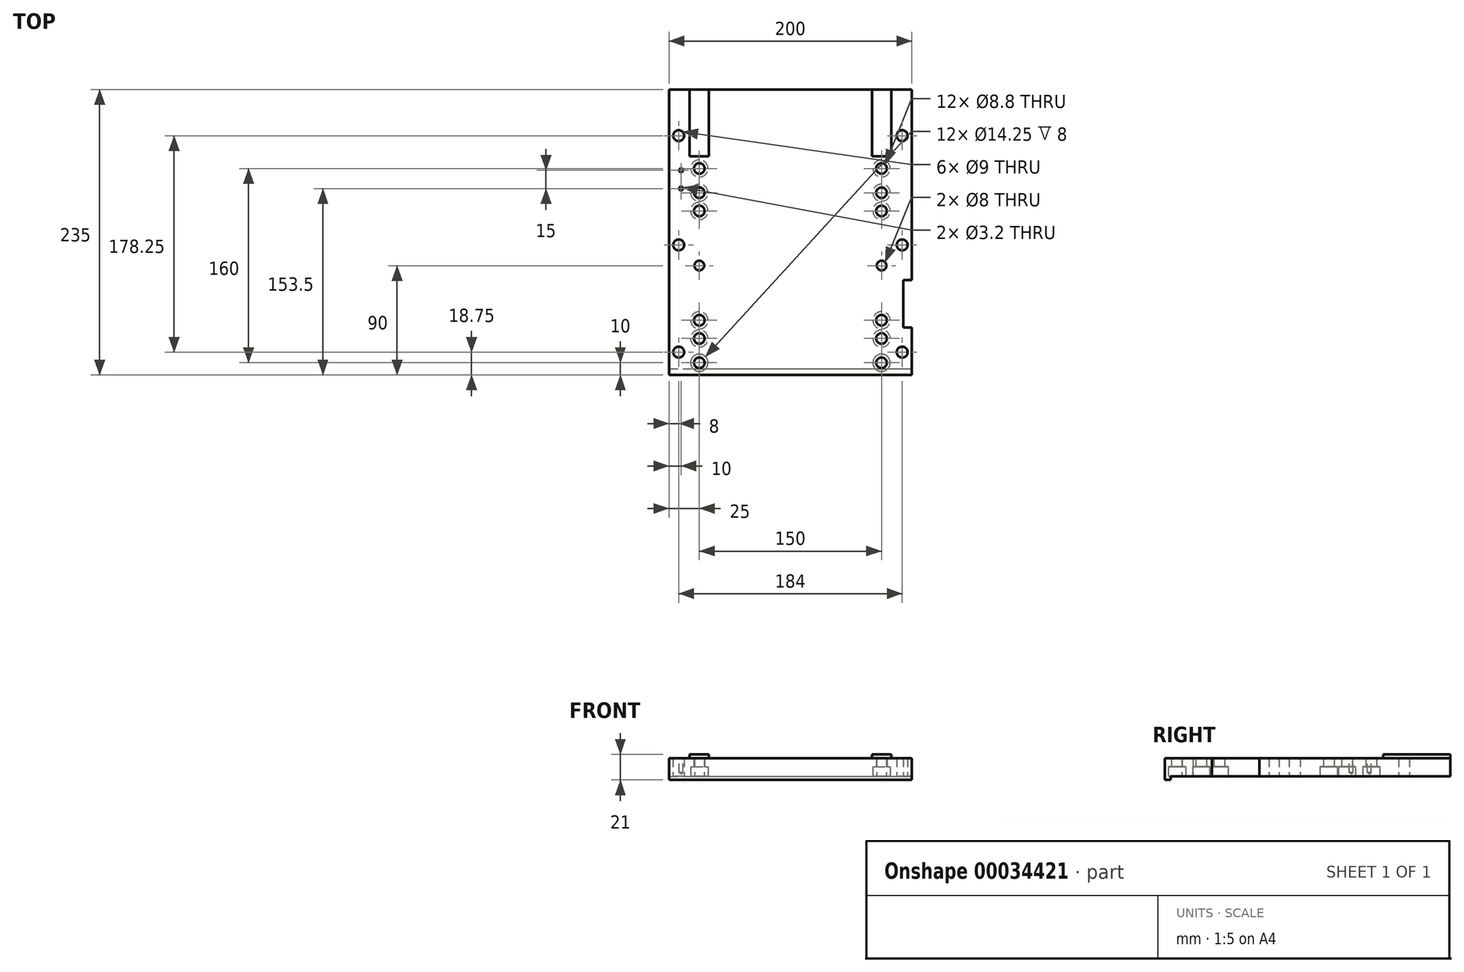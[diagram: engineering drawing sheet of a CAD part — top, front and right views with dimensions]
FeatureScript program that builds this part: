
annotation { "Feature Type Name" : "Feature", "Feature Type Description" : "" }
export const myFeature = defineFeature(function(context is Context, id is Id, definition is map)
    precondition{}
    {
        {
            var Q0;
            Q0=qCreatedBy(makeId("Top.planeOp"),FACE);
            var sketch = newSketch(context, id + "F0", { "sketchPlane" : qUnion([Q0])});
            skLineSegment(sketch, "E0", {"start": v(-100, 117.5) * mm, "end": v(100, 117.5) * mm});
            skLineSegment(sketch, "E1", {"start": v(-100, -117.5) * mm, "end": v(100, -117.5) * mm});
            skLineSegment(sketch, "E2", {"start": v(-100, -117.5) * mm, "end": v(-100, 117.5) * mm});
            skLineSegment(sketch, "E3", {"start": v(93, -78.5) * mm, "end": v(100, -78.5) * mm});
            skLineSegment(sketch, "E4", {"start": v(93, -39.5) * mm, "end": v(93, -78.5) * mm});
            skLineSegment(sketch, "E5", {"start": v(100, -39.5) * mm, "end": v(100, 117.5) * mm});
            skLineSegment(sketch, "E6", {"start": v(100, -117.5) * mm, "end": v(100, -78.5) * mm});
            skLineSegment(sketch, "E7", {"start": v(100, -39.5) * mm, "end": v(93, -39.5) * mm});
            skCircle(sketch, "E8", {"center": v(75, -27.5) * mm, "radius": 4 * mm});
            skCircle(sketch, "E9", {"center": v(92, -98.75) * mm, "radius": 4.5 * mm});
            skCircle(sketch, "E10", {"center": v(92, -10.5) * mm, "radius": 4.5 * mm});
            skCircle(sketch, "E11", {"center": v(92, 79.5) * mm, "radius": 4.5 * mm});
            skCircle(sketch, "E12", {"center": v(-92, 79.5) * mm, "radius": 4.5 * mm});
            skCircle(sketch, "E13", {"center": v(-92, -10.5) * mm, "radius": 4.5 * mm});
            skCircle(sketch, "E14", {"center": v(-92, -98.75) * mm, "radius": 4.5 * mm});
            skCircle(sketch, "E15", {"center": v(-75, -27.5) * mm, "radius": 4 * mm});
            skLineSegment(sketch, "E16", {"start": v(-83, 62.5) * mm, "end": v(-67, 62.5) * mm});
            skLineSegment(sketch, "E17", {"start": v(83, 117.5) * mm, "end": v(83, 62.5) * mm});
            skLineSegment(sketch, "E18", {"start": v(-83, 117.5) * mm, "end": v(-83, 62.5) * mm});
            skLineSegment(sketch, "E19", {"start": v(-100, -112.5) * mm, "end": v(100, -112.5) * mm});
            skLineSegment(sketch, "E20", {"start": v(-67, 117.5) * mm, "end": v(-67, 62.5) * mm});
            skLineSegment(sketch, "E21", {"start": v(67, 117.5) * mm, "end": v(67, 62.5) * mm});
            skLineSegment(sketch, "E22", {"start": v(67, 62.5) * mm, "end": v(83, 62.5) * mm});
            skSolve(sketch);
        }
        {
            var Q0;
            {var subQ7=sQuery(id+"F0.wireOp",EDGE,"E3");Q0=makeQuery(id+"F0.imprint","IMPRINT",FACE,{"disambiguationData":[TD([[makeQuery(id+"F0.imprint","IMPRINT",EDGE,{"derivedFrom":subQ7}),-1.0]])]});}
            var Q1;
            {var subQ0=sQuery(id+"F0.wireOp",EDGE,"E1");Q1=makeQuery(id+"F0.imprint","IMPRINT",FACE,{"disambiguationData":[TD([[makeQuery(id+"F0.imprint","IMPRINT",EDGE,{"derivedFrom":subQ0}),1.0]])]});}
            var Q2;
            Q2=makeQuery(id+"F0.imprint","IMPRINT",FACE,{"disambiguationData":[TD([[makeQuery(id+"F0.imprint","IMPRINT",EDGE,{"derivedFrom":sQuery(id+"F0.wireOp",EDGE,"E16")}),1.0]])]});
            var Q3;
            {var subQ0=sQuery(id+"F0.wireOp",EDGE,"E17");Q3=makeQuery(id+"F0.imprint","IMPRINT",FACE,{"disambiguationData":[TD([[makeQuery(id+"F0.imprint","IMPRINT",EDGE,{"derivedFrom":subQ0}),-1.0]])]});}
            extrude(context, id + "F1", {"entities" : qUnion([Q0, Q1, Q2, Q3]), "depth" : 15 * mm});
        }
        {
            var Q0;
            {var subQ0=sQuery(id+"F0.wireOp",EDGE,"E1");Q0=makeQuery(id+"F0.imprint","IMPRINT",FACE,{"disambiguationData":[TD([[makeQuery(id+"F0.imprint","IMPRINT",EDGE,{"derivedFrom":subQ0}),1.0]])]});}
            extrude(context, id + "F2", {"entities" : qUnion([Q0]), "operationType" : NewBodyOperationType.ADD, "oppositeDirection" : true, "depth" : 3 * mm});
        }
        {
            var Q0;
            {var subQ0=sQuery(id+"F0.wireOp",EDGE,"E17");Q0=makeQuery(id+"F0.imprint","IMPRINT",FACE,{"disambiguationData":[TD([[makeQuery(id+"F0.imprint","IMPRINT",EDGE,{"derivedFrom":subQ0}),-1.0]])]});}
            var Q1;
            Q1=makeQuery(id+"F0.imprint","IMPRINT",FACE,{"disambiguationData":[TD([[makeQuery(id+"F0.imprint","IMPRINT",EDGE,{"derivedFrom":sQuery(id+"F0.wireOp",EDGE,"E16")}),1.0]])]});
            extrude(context, id + "F3", {"entities" : qUnion([Q0, Q1]), "operationType" : NewBodyOperationType.ADD, "depth" : 18 * mm});
        }
        {
            var Q0;
            {var subQ7=sQuery(id+"F0.wireOp",EDGE,"E3");Q0=makeQuery(id+"F0.imprint","IMPRINT",FACE,{"disambiguationData":[TD([[makeQuery(id+"F0.imprint","IMPRINT",EDGE,{"derivedFrom":subQ7}),-1.0]])]});}
            var sketch = newSketch(context, id + "F4", { "sketchPlane" : qUnion([Q0])});
            skLineSegment(sketch, "E23.0", {"start": v(-100, -117.5) * mm, "end": v(100, -117.5) * mm, "construction": true});
            skLineSegment(sketch, "E24.0", {"start": v(100, -117.5) * mm, "end": v(100, -78.5) * mm, "construction": true});
            skPoint(sketch, "E25", {"position": v(75, -107.5) * mm});
            skPoint(sketch, "E26", {"position": v(75, -87.5) * mm});
            skPoint(sketch, "E27", {"position": v(75, -72.5) * mm});
            skPoint(sketch, "E28", {"position": v(-75, -107.5) * mm});
            skPoint(sketch, "E29", {"position": v(-75, -87.5) * mm});
            skPoint(sketch, "E30", {"position": v(-75, -72.5) * mm});
            skPoint(sketch, "E31", {"position": v(75, 17.5) * mm});
            skPoint(sketch, "E32", {"position": v(75, 32.5) * mm});
            skPoint(sketch, "E33", {"position": v(75, 52.5) * mm});
            skPoint(sketch, "E34", {"position": v(-75, 52.5) * mm});
            skPoint(sketch, "E35", {"position": v(-75, 32.5) * mm});
            skPoint(sketch, "E36", {"position": v(-75, 17.5) * mm});
            skSolve(sketch);
        }
        {
            var Q0;
            Q0=sQuery(id+"F4.wireOp",VERTEX,"E25");
            var Q1;
            Q1=sQuery(id+"F4.wireOp",VERTEX,"E26");
            var Q2;
            Q2=sQuery(id+"F4.wireOp",VERTEX,"E27");
            var Q3;
            Q3=sQuery(id+"F4.wireOp",VERTEX,"E31");
            var Q4;
            Q4=sQuery(id+"F4.wireOp",VERTEX,"E32");
            var Q5;
            Q5=sQuery(id+"F4.wireOp",VERTEX,"E33");
            var Q6;
            Q6=sQuery(id+"F4.wireOp",VERTEX,"E34");
            var Q7;
            Q7=sQuery(id+"F4.wireOp",VERTEX,"E35");
            var Q8;
            Q8=sQuery(id+"F4.wireOp",VERTEX,"E36");
            var Q9;
            Q9=sQuery(id+"F4.wireOp",VERTEX,"E30");
            var Q10;
            Q10=sQuery(id+"F4.wireOp",VERTEX,"E29");
            var Q11;
            Q11=sQuery(id+"F4.wireOp",VERTEX,"E28");
            var Q12;
            Q12=makeQuery(id+"F1.opExtrude","SWEPT_BODY",BODY,{"disambiguationData":[OSD([sQuery(id+"F0.wireOp",EDGE,"E0"),sQuery(id+"F0.wireOp",EDGE,"E1"),sQuery(id+"F0.wireOp",EDGE,"E2"),sQuery(id+"F0.wireOp",EDGE,"E3"),sQuery(id+"F0.wireOp",EDGE,"E4"),sQuery(id+"F0.wireOp",EDGE,"E5"),sQuery(id+"F0.wireOp",EDGE,"E6"),sQuery(id+"F0.wireOp",EDGE,"E7"),sQuery(id+"F0.wireOp",EDGE,"E8"),sQuery(id+"F0.wireOp",EDGE,"E9"),sQuery(id+"F0.wireOp",EDGE,"E10"),sQuery(id+"F0.wireOp",EDGE,"E11"),sQuery(id+"F0.wireOp",EDGE,"E12"),sQuery(id+"F0.wireOp",EDGE,"E13"),sQuery(id+"F0.wireOp",EDGE,"E14"),sQuery(id+"F0.wireOp",EDGE,"E15")])]});
            hole(context, id + "F5", {"style" : HoleStyle.C_BORE, "endStyle" : HoleEndStyle.THROUGH, "oppositeDirection" : true, "standardTappedOrClearance" : lookupTablePath({ "standard" : "ISO", "fit" : "Normal", "size" : "M8", "type" : "Clearance" }), "standardBlindInLast" : lookupTablePath({ "fit" : "Standard", "standard" : "ISO", "size" : "M8", "type" : "Clearance" }), "holeDiameter" : 8.8 * mm, "cBoreDiameter" : 14.25 * mm, "cBoreDepth" : 8 * mm, "tappedDepth" : 12 * mm, "tapClearance" : 3, "locations" : qUnion([Q0, Q1, Q2, Q3, Q4, Q5, Q6, Q7, Q8, Q9, Q10, Q11]), "scope" : qUnion([Q12])});
        }
        {
            var Q0;
            Q0=makeQuery(id+"F1.opExtrude","CAP_FACE",FACE,{"disambiguationData":[OSD([sQuery(id+"F0.wireOp",EDGE,"E0"),sQuery(id+"F0.wireOp",EDGE,"E1"),sQuery(id+"F0.wireOp",EDGE,"E2"),sQuery(id+"F0.wireOp",EDGE,"E3"),sQuery(id+"F0.wireOp",EDGE,"E4"),sQuery(id+"F0.wireOp",EDGE,"E5"),sQuery(id+"F0.wireOp",EDGE,"E6"),sQuery(id+"F0.wireOp",EDGE,"E7"),sQuery(id+"F0.wireOp",EDGE,"E8"),sQuery(id+"F0.wireOp",EDGE,"E9"),sQuery(id+"F0.wireOp",EDGE,"E10"),sQuery(id+"F0.wireOp",EDGE,"E11"),sQuery(id+"F0.wireOp",EDGE,"E12"),sQuery(id+"F0.wireOp",EDGE,"E13"),sQuery(id+"F0.wireOp",EDGE,"E14"),sQuery(id+"F0.wireOp",EDGE,"E15")])],"isStart":false});
            var sketch = newSketch(context, id + "F6", { "sketchPlane" : qUnion([Q0])});
            skPoint(sketch, "E37", {"position": v(-90, 36) * mm});
            skPoint(sketch, "E38", {"position": v(-90, 51) * mm});
            skSolve(sketch);
        }
        {
            var Q0;
            Q0=sQuery(id+"F6.wireOp",VERTEX,"E38");
            var Q1;
            Q1=sQuery(id+"F6.wireOp",VERTEX,"E37");
            var Q2;
            Q2=makeQuery(id+"F1.opExtrude","SWEPT_BODY",BODY,{"disambiguationData":[OSD([sQuery(id+"F0.wireOp",EDGE,"E0"),sQuery(id+"F0.wireOp",EDGE,"E1"),sQuery(id+"F0.wireOp",EDGE,"E2"),sQuery(id+"F0.wireOp",EDGE,"E3"),sQuery(id+"F0.wireOp",EDGE,"E4"),sQuery(id+"F0.wireOp",EDGE,"E5"),sQuery(id+"F0.wireOp",EDGE,"E6"),sQuery(id+"F0.wireOp",EDGE,"E7"),sQuery(id+"F0.wireOp",EDGE,"E8"),sQuery(id+"F0.wireOp",EDGE,"E9"),sQuery(id+"F0.wireOp",EDGE,"E10"),sQuery(id+"F0.wireOp",EDGE,"E11"),sQuery(id+"F0.wireOp",EDGE,"E12"),sQuery(id+"F0.wireOp",EDGE,"E13"),sQuery(id+"F0.wireOp",EDGE,"E14"),sQuery(id+"F0.wireOp",EDGE,"E15")])]});
            hole(context, id + "F7", {"style" : HoleStyle.SIMPLE, "endStyle" : HoleEndStyle.BLIND, "standardTappedOrClearance" : lookupTablePath({ "standard" : "ISO", "engagement" : "75%", "pitch" : "0.75 mm", "size" : "M4", "type" : "Tapped" }), "standardBlindInLast" : lookupTablePath({ "standard" : "ISO", "engagement" : "75%", "pitch" : "0.75 mm", "size" : "M4", "type" : "Tapped" }), "holeDiameter" : 3.2 * mm, "showTappedDepth" : true, "holeDepth" : 12 * mm, "tappedDepth" : 9.75 * mm, "tapClearance" : 3, "locations" : qUnion([Q0, Q1]), "scope" : qUnion([Q2])});
        }
    });
